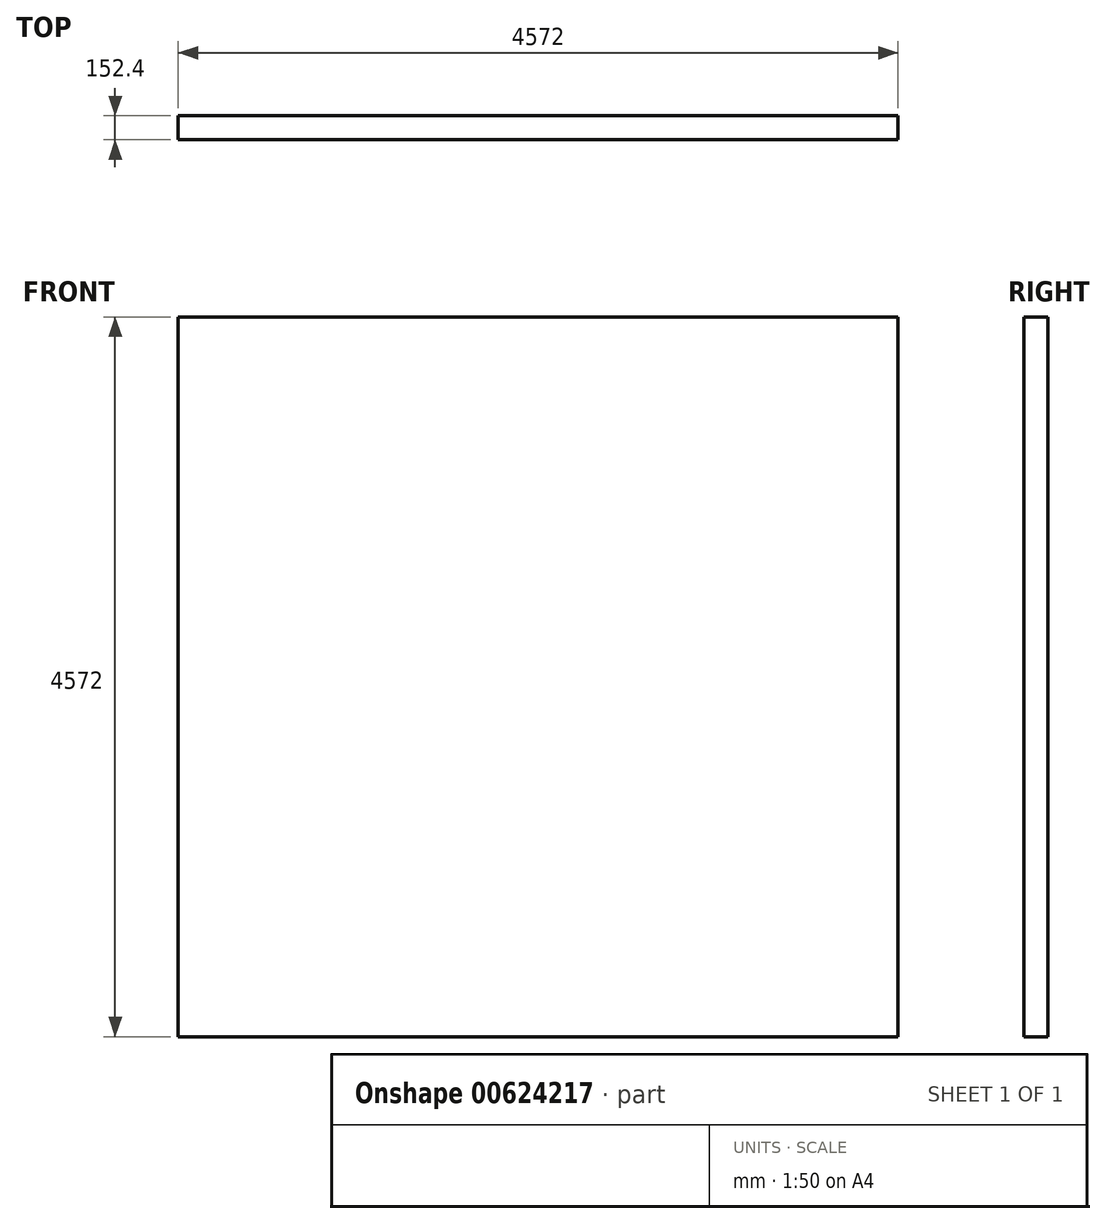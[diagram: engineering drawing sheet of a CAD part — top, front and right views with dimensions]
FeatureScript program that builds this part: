
annotation { "Feature Type Name" : "Feature", "Feature Type Description" : "" }
export const myFeature = defineFeature(function(context is Context, id is Id, definition is map)
    precondition{}
    {
        {
            var Q0;
            Q0=qCreatedBy(makeId("Front.planeOp"),FACE);
            var sketch = newSketch(context, id + "F0", { "sketchPlane" : qUnion([Q0])});
            skLineSegment(sketch, "E0.bottom", {"start": v(-2285.99, 2419.85) * mm, "end": v(2286.01, 2419.85) * mm});
            skLineSegment(sketch, "E0.top", {"start": v(-2285.99, -2152.15) * mm, "end": v(2286.01, -2152.15) * mm});
            skLineSegment(sketch, "E0.left", {"start": v(-2285.99, 2419.85) * mm, "end": v(-2285.99, -2152.15) * mm});
            skLineSegment(sketch, "E0.right", {"start": v(2286.01, 2419.85) * mm, "end": v(2286.01, -2152.15) * mm});
            skSolve(sketch);
        }
        {
            var Q0;
            Q0 = qSketchRegion(id + "F0", true);
            extrude(context, id + "F1", {"entities" : qUnion([Q0]), "depth" : 152.4 * mm, "offsetDistance" : 30.48 * mm});
        }
    });
